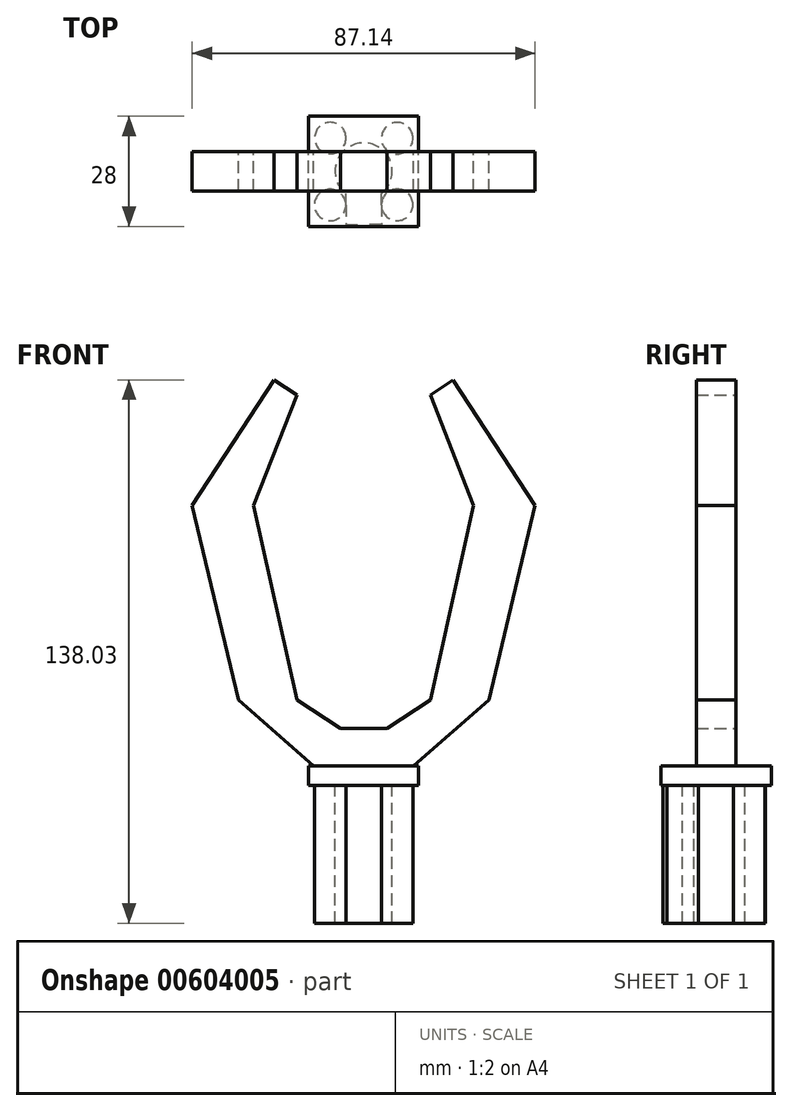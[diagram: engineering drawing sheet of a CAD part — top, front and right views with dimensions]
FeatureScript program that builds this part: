
annotation { "Feature Type Name" : "Feature", "Feature Type Description" : "" }
export const myFeature = defineFeature(function(context is Context, id is Id, definition is map)
    precondition{}
    {
        {
            var Q0;
            Q0=qCreatedBy(makeId("Front.planeOp"),FACE);
            var sketch = newSketch(context, id + "F0", { "sketchPlane" : qUnion([Q0])});
            skLineSegment(sketch, "E0", {"start": v(0, 0) * mm, "end": v(-12.7, 0) * mm});
            skLineSegment(sketch, "E1", {"start": v(0, 0) * mm, "end": v(12.7, 0) * mm});
            skLineSegment(sketch, "E2", {"start": v(-12.7, 0) * mm, "end": v(-31.83, 16.7) * mm});
            skLineSegment(sketch, "E3", {"start": v(-31.83, 16.7) * mm, "end": v(-43.57, 66.13) * mm});
            skLineSegment(sketch, "E4", {"start": v(-43.57, 66.13) * mm, "end": v(-22.73, 98.03) * mm});
            skLineSegment(sketch, "E5", {"start": v(-22.73, 98.03) * mm, "end": v(-16.97, 94.27) * mm});
            skLineSegment(sketch, "E6", {"start": v(-16.97, 94.27) * mm, "end": v(-27.92, 66.13) * mm});
            skLineSegment(sketch, "E7", {"start": v(-27.92, 66.13) * mm, "end": v(-16.97, 16.7) * mm});
            skLineSegment(sketch, "E8", {"start": v(-16.97, 16.7) * mm, "end": v(-5.88, 9.47) * mm});
            skLineSegment(sketch, "E9", {"start": v(-5.88, 9.47) * mm, "end": v(0, 9.47) * mm});
            skLineSegment(sketch, "E10.MirrorCS", {"start": v(16.97, 94.27) * mm, "end": v(27.92, 66.13) * mm});
            skLineSegment(sketch, "E11.MirrorCS", {"start": v(43.57, 66.13) * mm, "end": v(22.73, 98.03) * mm});
            skLineSegment(sketch, "E12.MirrorCS", {"start": v(22.73, 98.03) * mm, "end": v(16.97, 94.27) * mm});
            skLineSegment(sketch, "E13.MirrorCS", {"start": v(31.83, 16.7) * mm, "end": v(43.57, 66.13) * mm});
            skLineSegment(sketch, "E14.MirrorCS", {"start": v(27.92, 66.13) * mm, "end": v(16.97, 16.7) * mm});
            skLineSegment(sketch, "E15.MirrorCS", {"start": v(16.97, 16.7) * mm, "end": v(5.88, 9.47) * mm});
            skLineSegment(sketch, "E16.MirrorCS", {"start": v(5.88, 9.47) * mm, "end": v(0, 9.47) * mm});
            skLineSegment(sketch, "E17.MirrorCS", {"start": v(12.7, 0) * mm, "end": v(31.83, 16.7) * mm});
            skSolve(sketch);
        }
        {
            var Q0;
            Q0 = qSketchRegion(id + "F0", true);
            extrude(context, id + "F1", {"entities" : qUnion([Q0]), "depth" : 10 * mm, "offsetDistance" : 25.4 * mm});
        }
        {
            var Q0;
            Q0=makeQuery(id+"F1.opExtrude","SWEPT_FACE",FACE,{"disambiguationData":[OSD([sQuery(id+"F0.wireOp",EDGE,"E0"),sQuery(id+"F0.wireOp",EDGE,"E1")])]});
            cPlane(context, id + "F2", {"entities" : qUnion([Q0]), "cplaneType" : CPlaneType.OFFSET, "offset" : 0 * mm, "width" : 152.4 * mm, "height" : 152.4 * mm});
        }
        {
            var Q0;
            Q0=qCreatedBy(id+"F2.planeOp",FACE);
            var sketch = newSketch(context, id + "F3", { "sketchPlane" : qUnion([Q0])});
            skLineSegment(sketch, "E18", {"start": v(0, 0) * mm, "end": v(0, 5) * mm});
            skLineSegment(sketch, "E19", {"start": v(0, 5) * mm, "end": v(-14, 5) * mm});
            skLineSegment(sketch, "E20", {"start": v(-14, 5) * mm, "end": v(-14, 19) * mm});
            skLineSegment(sketch, "E21", {"start": v(-14, 5) * mm, "end": v(-14, -9) * mm});
            skLineSegment(sketch, "E22", {"start": v(-14, 19) * mm, "end": v(0, 19) * mm});
            skLineSegment(sketch, "E23", {"start": v(-14, -9) * mm, "end": v(0, -9) * mm});
            skLineSegment(sketch, "E24", {"start": v(0, -9) * mm, "end": v(0, 19) * mm});
            skLineSegment(sketch, "E25.MirrorCS", {"start": v(14, 19) * mm, "end": v(0, 19) * mm});
            skLineSegment(sketch, "E26.MirrorCS", {"start": v(14, 5) * mm, "end": v(14, 19) * mm});
            skLineSegment(sketch, "E27.MirrorCS", {"start": v(14, 5) * mm, "end": v(14, -9) * mm});
            skLineSegment(sketch, "E28.MirrorCS", {"start": v(14, -9) * mm, "end": v(0, -9) * mm});
            skSolve(sketch);
        }
        {
            var Q0;
            {var subQ0=sQuery(id+"F3.wireOp",EDGE,"E19");var subQ1=makeQuery(id+"F3.imprint","IMPRINT",EDGE,{"derivedFrom":subQ0});var subQ3=sQuery(id+"F3.wireOp",EDGE,"E18");var subQ10=makeQuery(id+"F3.imprint","IMPRINT",EDGE,{"derivedFrom":subQ3});Q0=qUnion([makeQuery(id+"F3.imprint","IMPRINT",FACE,{"disambiguationData":[TD([[subQ10,1.0]])]}),makeQuery(id+"F3.imprint","IMPRINT",FACE,{"disambiguationData":[TD([[subQ10,-1.0]])]}),makeQuery(id+"F3.imprint","IMPRINT",FACE,{"disambiguationData":[TD([[subQ1,-1.0]])]})]);}
            extrude(context, id + "F4", {"entities" : qUnion([Q0]), "operationType" : NewBodyOperationType.ADD, "depth" : 5 * mm, "offsetDistance" : 25.4 * mm});
        }
        {
            var Q0;
            Q0=makeQuery(id+"F4.opExtrude","CAP_FACE",FACE,{"disambiguationData":[OSD([sQuery(id+"F3.wireOp",EDGE,"E20"),sQuery(id+"F3.wireOp",EDGE,"E21"),sQuery(id+"F3.wireOp",EDGE,"E22"),sQuery(id+"F3.wireOp",EDGE,"E23"),sQuery(id+"F3.wireOp",EDGE,"E25.MirrorCS"),sQuery(id+"F3.wireOp",EDGE,"E26.MirrorCS"),sQuery(id+"F3.wireOp",EDGE,"E27.MirrorCS"),sQuery(id+"F3.wireOp",EDGE,"E28.MirrorCS")])],"isStart":false});
            cPlane(context, id + "F5", {"entities" : qUnion([Q0]), "cplaneType" : CPlaneType.OFFSET, "offset" : 0 * mm, "width" : 152.4 * mm, "height" : 152.4 * mm});
        }
        {
            var Q0;
            Q0=qCreatedBy(id+"F5.planeOp",FACE);
            var sketch = newSketch(context, id + "F6", { "sketchPlane" : qUnion([Q0])});
            skLineSegment(sketch, "E29", {"start": v(0, -2.25) * mm, "end": v(0, -5) * mm});
            skLineSegment(sketch, "E30", {"start": v(0, 5) * mm, "end": v(0, 5) * mm});
            skLineSegment(sketch, "E31", {"start": v(-4.51, 15) * mm, "end": v(-4.8, 15) * mm});
            skLineSegment(sketch, "E32", {"start": v(0, -5) * mm, "end": v(-4.77, -5) * mm});
            skLineSegment(sketch, "E33", {"start": v(-12.7, 15) * mm, "end": v(-12.7, -5) * mm});
            skLineSegment(sketch, "E34.MirrorCS", {"start": v(12.7, 15) * mm, "end": v(12.7, -5) * mm});
            skLineSegment(sketch, "E35.MirrorCS", {"start": v(4.51, 15) * mm, "end": v(4.82, 15) * mm});
            skLineSegment(sketch, "E36.MirrorCS", {"start": v(0, -5) * mm, "end": v(4.86, -5) * mm});
            skLineSegment(sketch, "E37", {"start": v(-12.7, 15) * mm, "end": v(-12.33, 14.72) * mm});
            skLineSegment(sketch, "E38", {"start": v(12.7, 15) * mm, "end": v(12.34, 14.72) * mm});
            skCircle(sketch, "E39", {"center": v(-8.51, 13.54) * mm, "radius": 4 * mm});
            skCircle(sketch, "E40", {"center": v(8.53, 13.5) * mm, "radius": 4 * mm});
            skCircle(sketch, "E41", {"center": v(-8.46, -3.46) * mm, "radius": 4 * mm});
            skCircle(sketch, "E42", {"center": v(8.54, -3.42) * mm, "radius": 4 * mm});
            skLineSegment(sketch, "E43", {"start": v(-8.5, 9.54) * mm, "end": v(-8.47, 0.54) * mm});
            skLineSegment(sketch, "E44", {"start": v(-4.46, -3.45) * mm, "end": v(4.54, -3.43) * mm});
            skLineSegment(sketch, "E45", {"start": v(8.53, 0.58) * mm, "end": v(8.53, 9.5) * mm});
            skLineSegment(sketch, "E46", {"start": v(-4.51, 13.55) * mm, "end": v(-4.52, 18.55) * mm});
            skLineSegment(sketch, "E47", {"start": v(-4.52, 18.55) * mm, "end": v(0, 18.56) * mm});
            skLineSegment(sketch, "E48.MirrorCS", {"start": v(4.52, 18.55) * mm, "end": v(0, 18.56) * mm});
            skLineSegment(sketch, "E49.MirrorCS", {"start": v(4.51, 13.55) * mm, "end": v(4.52, 18.55) * mm});
            skArc(sketch, "E50", {"start": v(-4.51, 10.68) * mm, "mid": v(0, -2.25) * mm, "end": v(4.51, 10.68) * mm});
            skLineSegment(sketch, "E51", {"start": v(-4.51, 13.55) * mm, "end": v(-4.51, 10.68) * mm});
            skLineSegment(sketch, "E52", {"start": v(4.51, 13.55) * mm, "end": v(4.51, 10.68) * mm});
            skLineSegment(sketch, "E53.trimOffspring", {"start": v(-6.47, 10.1) * mm, "end": v(-5.7, 9.5) * mm});
            skLineSegment(sketch, "E54.trimOffspring", {"start": v(-12.23, 15) * mm, "end": v(-12.7, 15) * mm});
            skLineSegment(sketch, "E55.trimOffspring", {"start": v(12.23, 15) * mm, "end": v(12.7, 15) * mm});
            skLineSegment(sketch, "E56.trimOffspring", {"start": v(6.45, 10.08) * mm, "end": v(5.7, 9.5) * mm});
            skLineSegment(sketch, "E57.trimOffspring", {"start": v(12.32, -4.7) * mm, "end": v(12.7, -5) * mm});
            skLineSegment(sketch, "E58.trimOffspring", {"start": v(-5.7, 0.51) * mm, "end": v(-6.4, -0.04) * mm});
            skLineSegment(sketch, "E59.trimOffspring", {"start": v(5.7, 0.51) * mm, "end": v(6.4, -0.04) * mm});
            skLineSegment(sketch, "E60.trimOffspring", {"start": v(-12.28, -4.67) * mm, "end": v(-12.7, -5) * mm});
            skPoint(sketch, "E61.orphan", {"position": v(0, 15) * mm});
            skPoint(sketch, "E62.MirrorCS.start.orphan", {"position": v(0, 0) * mm});
            skLineSegment(sketch, "E63.trimOffspring", {"start": v(-12.16, -5) * mm, "end": v(-12.7, -5) * mm});
            skLineSegment(sketch, "E64.trimOffspring", {"start": v(12.2, -5) * mm, "end": v(12.7, -5) * mm});
            skSolve(sketch);
        }
        {
            var Q0;
            {var subQ0=sQuery(id+"F6.wireOp",EDGE,"E39");var subQ4=makeQuery(id+"F6.imprint","INTERSECT",VERTEX,{"derivedFrom":[sQuery(id+"F6.wireOp",EDGE,"E31"),subQ0]});Q0=makeQuery(id+"F6.imprint","IMPRINT",FACE,{"disambiguationData":[TD([[makeQuery(id+"F6.imprint","IMPRINT",EDGE,{"disambiguationData":[TD([[subQ4,1.0]])],"derivedFrom":subQ0}),1.0]])]});}
            var Q1;
            {var subQ0=sQuery(id+"F6.wireOp",EDGE,"E41");var subQ5=makeQuery(id+"F6.imprint","INTERSECT",VERTEX,{"derivedFrom":[subQ0,sQuery(id+"F6.wireOp",EDGE,"E44")]});Q1=makeQuery(id+"F6.imprint","IMPRINT",FACE,{"disambiguationData":[TD([[makeQuery(id+"F6.imprint","IMPRINT",EDGE,{"disambiguationData":[TD([[subQ5,-1.0]])],"derivedFrom":subQ0}),1.0]])]});}
            var Q2;
            {var subQ13=sQuery(id+"F6.wireOp",EDGE,"E47");Q2=makeQuery(id+"F6.imprint","IMPRINT",FACE,{"disambiguationData":[TD([[makeQuery(id+"F6.imprint","IMPRINT",EDGE,{"derivedFrom":subQ13}),-1.0]])]});}
            var Q3;
            {var subQ0=sQuery(id+"F6.wireOp",EDGE,"E42");var subQ5=makeQuery(id+"F6.imprint","INTERSECT",VERTEX,{"derivedFrom":[subQ0,sQuery(id+"F6.wireOp",EDGE,"E45")]});Q3=makeQuery(id+"F6.imprint","IMPRINT",FACE,{"disambiguationData":[TD([[makeQuery(id+"F6.imprint","IMPRINT",EDGE,{"disambiguationData":[TD([[subQ5,-1.0]])],"derivedFrom":subQ0}),1.0]])]});}
            var Q4;
            {var subQ0=sQuery(id+"F6.wireOp",EDGE,"E40");var subQ5=makeQuery(id+"F6.imprint","INTERSECT",VERTEX,{"derivedFrom":[sQuery(id+"F6.wireOp",EDGE,"E38"),subQ0]});Q4=makeQuery(id+"F6.imprint","IMPRINT",FACE,{"disambiguationData":[TD([[makeQuery(id+"F6.imprint","IMPRINT",EDGE,{"disambiguationData":[TD([[subQ5,-1.0]])],"derivedFrom":subQ0}),1.0]])]});}
            extrude(context, id + "F7", {"entities" : qUnion([Q0, Q1, Q2, Q3, Q4]), "operationType" : NewBodyOperationType.ADD, "depth" : 35 * mm, "offsetDistance" : 25.4 * mm});
        }
    });
